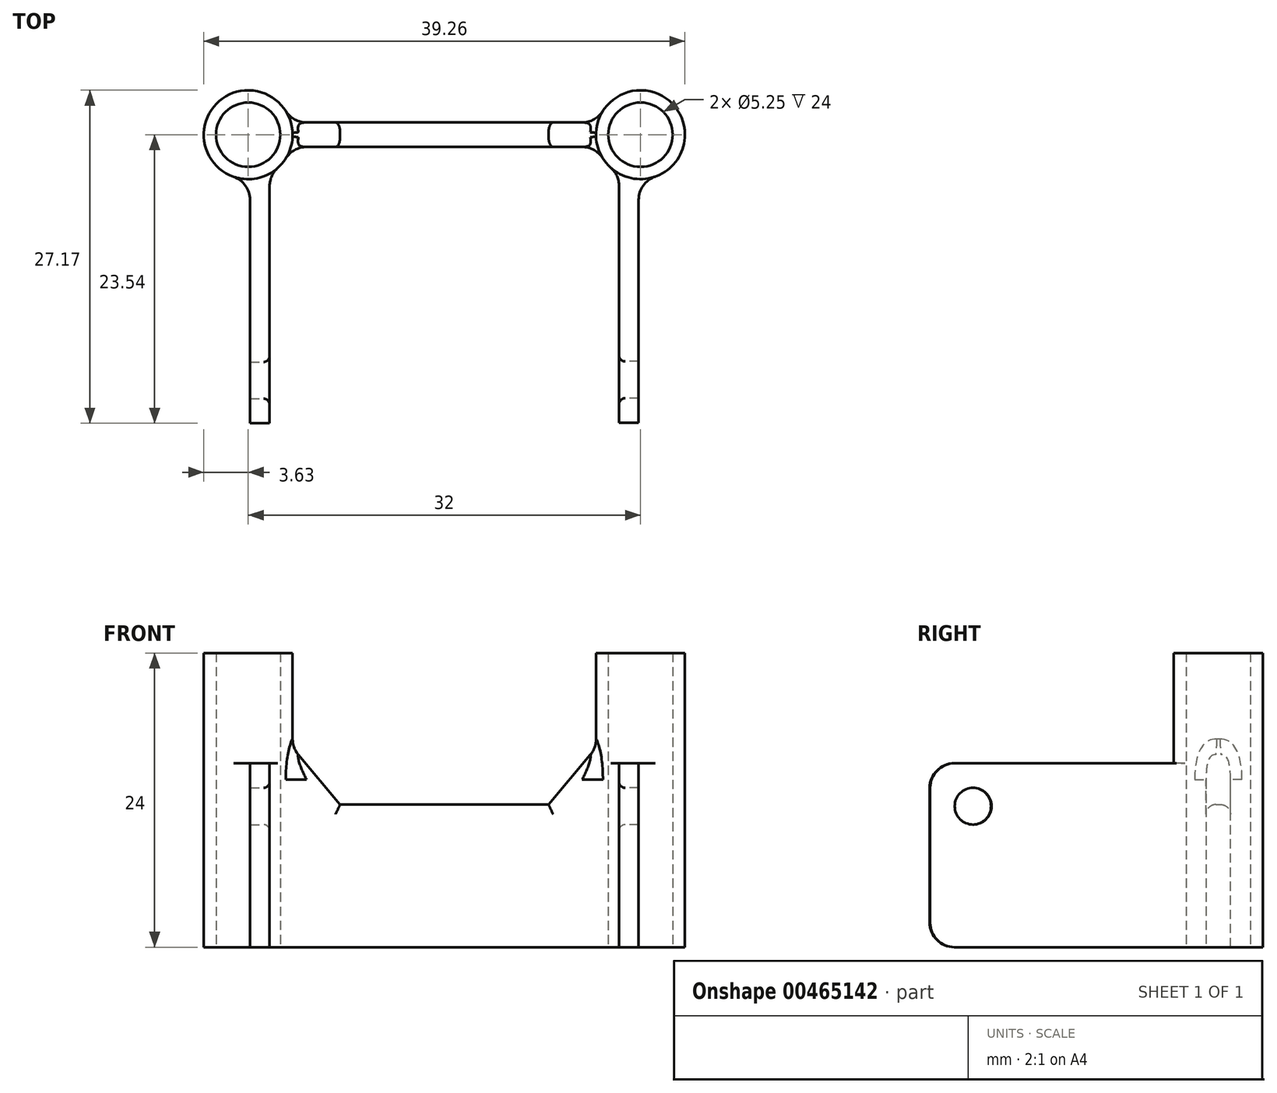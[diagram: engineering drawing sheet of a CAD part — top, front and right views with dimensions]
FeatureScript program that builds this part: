
annotation { "Feature Type Name" : "Feature", "Feature Type Description" : "" }
export const myFeature = defineFeature(function(context is Context, id is Id, definition is map)
    precondition{}
    {
        {
            var Q0;
            Q0=qCreatedBy(makeId("Top.planeOp"),FACE);
            var sketch = newSketch(context, id + "F0", { "sketchPlane" : qUnion([Q0])});
            skCircle(sketch, "E0", {"center": v(-16, 0) * mm, "radius": 3.62 * mm});
            skCircle(sketch, "E1", {"center": v(16, 0) * mm, "radius": 3.62 * mm});
            skSolve(sketch);
        }
        {
            var Q0;
            Q0=qSketchRegion(id+"F0",true);
            extrude(context, id + "F1", {"entities" : qUnion([Q0]), "depth" : 24 * mm});
        }
        {
            var Q0;
            Q0=qCreatedBy(makeId("Front.planeOp"),FACE);
            var sketch = newSketch(context, id + "F2", { "sketchPlane" : qUnion([Q0])});
            skLineSegment(sketch, "E2", {"start": v(13, 0) * mm, "end": v(13, 17) * mm});
            skLineSegment(sketch, "E3", {"start": v(13, 17) * mm, "end": v(13, 17) * mm});
            skLineSegment(sketch, "E4", {"start": v(13, 17) * mm, "end": v(8.5, 11.64) * mm});
            skLineSegment(sketch, "E5", {"start": v(8.5, 11.64) * mm, "end": v(-8.5, 11.64) * mm});
            skLineSegment(sketch, "E6", {"start": v(-8.5, 11.64) * mm, "end": v(-13, 17) * mm});
            skLineSegment(sketch, "E7", {"start": v(-13, 17) * mm, "end": v(-13, 0) * mm});
            skLineSegment(sketch, "E8", {"start": v(-13, 0) * mm, "end": v(13, 0) * mm});
            skSolve(sketch);
        }
        {
            var Q0;
            Q0=makeQuery(id+"F2.imprint","IMPRINT",FACE,{"disambiguationData":[TD([[makeQuery(id+"F2.imprint","IMPRINT",EDGE,{"derivedFrom":sQuery(id+"F2.wireOp",EDGE,"E2")}),1.0]])]});
            extrude(context, id + "F3", {"entities" : qUnion([Q0]), "endBound" : BoundingType.SYMMETRIC, "depth" : 2 * mm});
        }
        {
            var Q0;
            Q0=qCreatedBy(makeId("Right.planeOp"),FACE);
            var Q1;
            Q1=qBodyType(qCreatedBy(id+"F5",EDGE),BodyType.WIRE);
            cPlane(context, id + "F4", {"entities" : qUnion([Q0, Q1]), "cplaneType" : CPlaneType.OFFSET, "offset" : 14.25 * mm, "width" : 150 * mm, "height" : 150 * mm});
        }
        {
            var Q0;
            Q0=qCreatedBy(id+"F4.planeOp",FACE);
            var sketch = newSketch(context, id + "F5", { "sketchPlane" : qUnion([Q0])});
            skCircle(sketch, "E9", {"center": v(-20, 11.5) * mm, "radius": 1.5 * mm});
            skLineSegment(sketch, "E10", {"start": v(0, 0) * mm, "end": v(-21.5, 0) * mm});
            skLineSegment(sketch, "E11", {"start": v(-23.5, 2) * mm, "end": v(-23.5, 13) * mm});
            skLineSegment(sketch, "E12", {"start": v(-21.5, 15) * mm, "end": v(0, 15) * mm});
            skLineSegment(sketch, "E13", {"start": v(0, 15) * mm, "end": v(0, 0) * mm});
            skPoint(sketch, "E14.visualSharp", {"position": v(-23.5, 15) * mm});
            skArc(sketch, "E14.filletArc", {"start": v(-21.5, 15) * mm, "mid": v(-22.91, 14.41) * mm, "end": v(-23.5, 13) * mm});
            skPoint(sketch, "E15.visualSharp", {"position": v(-23.5, 0) * mm});
            skArc(sketch, "E15.filletArc", {"start": v(-23.5, 2) * mm, "mid": v(-22.91, 0.59) * mm, "end": v(-21.5, 0) * mm});
            skSolve(sketch);
        }
        {
            var Q0;
            Q0=qSketchRegion(id+"F5",true);
            extrude(context, id + "F6", {"entities" : qUnion([Q0]), "operationType" : NewBodyOperationType.ADD, "depth" : 1.6 * mm});
        }
        {
            var Q0;
            Q0=qCreatedBy(makeId("Right.planeOp"),FACE);
            cPlane(context, id + "F7", {"entities" : qUnion([Q0]), "cplaneType" : CPlaneType.OFFSET, "offset" : 14.25 * mm, "oppositeDirection" : true, "width" : 150 * mm, "height" : 150 * mm});
        }
        {
            var Q0;
            Q0=qCreatedBy(id+"F7.planeOp",FACE);
            var sketch = newSketch(context, id + "F8", { "sketchPlane" : qUnion([Q0])});
            skCircle(sketch, "E16", {"center": v(-20.04, 11.5) * mm, "radius": 1.5 * mm});
            skLineSegment(sketch, "E17", {"start": v(-0.04, 0) * mm, "end": v(-21.54, 0) * mm});
            skLineSegment(sketch, "E18", {"start": v(-23.54, 2) * mm, "end": v(-23.54, 13) * mm});
            skLineSegment(sketch, "E19", {"start": v(-21.54, 15) * mm, "end": v(-0.04, 15) * mm});
            skLineSegment(sketch, "E20", {"start": v(-0.04, 15) * mm, "end": v(-0.04, 0) * mm});
            skPoint(sketch, "E21.visualSharp", {"position": v(-23.54, 15) * mm});
            skArc(sketch, "E21.filletArc", {"start": v(-21.54, 15) * mm, "mid": v(-22.95, 14.41) * mm, "end": v(-23.54, 13) * mm});
            skPoint(sketch, "E22.visualSharp", {"position": v(-23.54, 0) * mm});
            skArc(sketch, "E22.filletArc", {"start": v(-23.54, 2) * mm, "mid": v(-22.95, 0.59) * mm, "end": v(-21.54, 0) * mm});
            skSolve(sketch);
        }
        {
            var Q0;
            Q0=qSketchRegion(id+"F8",true);
            extrude(context, id + "F9", {"entities" : qUnion([Q0]), "operationType" : NewBodyOperationType.ADD, "oppositeDirection" : true, "depth" : 1.6 * mm});
        }
        {
            var Q0;
            Q0=qCreatedBy(makeId("Top.planeOp"),FACE);
            var sketch = newSketch(context, id + "F10", { "sketchPlane" : qUnion([Q0])});
            skCircle(sketch, "E23", {"center": v(-16, 0) * mm, "radius": 0.5 * mm});
            skCircle(sketch, "E24", {"center": v(16, 0) * mm, "radius": 1.75 * mm});
            skSolve(sketch);
        }
        {
            var Q0;
            Q0=sQuery(id+"F10.wireOp",VERTEX,"E23.center");
            var Q1;
            Q1=sQuery(id+"F10.wireOp",VERTEX,"E24.center");
            var Q2;
            Q2=makeQuery(id+"F1.opExtrude","SWEPT_BODY",BODY,{"disambiguationData":[OSD([sQuery(id+"F0.wireOp",EDGE,"E0")])]});
            var Q3;
            Q3=makeQuery(id+"F3.opExtrude","SWEPT_BODY",BODY,{"disambiguationData":[OSD([sQuery(id+"F2.wireOp",EDGE,"in345Lub-D59E-tOme-60dj-Cq3KucnByxKd"),sQuery(id+"F2.wireOp",EDGE,"E2"),sQuery(id+"F2.wireOp",EDGE,"E4"),sQuery(id+"F2.wireOp",EDGE,"E5"),sQuery(id+"F2.wireOp",EDGE,"E6"),sQuery(id+"F2.wireOp",EDGE,"E7")])]});
            var Q4;
            Q4=makeQuery(id+"FYRTTrcSvXfLMjP_3.opExtrude","SWEPT_BODY",BODY,{"disambiguationData":[OSD([sQuery(id+"Fs8EBPNxBlUYa75_3.wireOp",EDGE,"JWLeMf17-8jiZ-tYXv-UtJK-ccR32AaEOkmf.bottom"),sQuery(id+"Fs8EBPNxBlUYa75_3.wireOp",EDGE,"JWLeMf17-8jiZ-tYXv-UtJK-ccR32AaEOkmf.top"),sQuery(id+"Fs8EBPNxBlUYa75_3.wireOp",EDGE,"JWLeMf17-8jiZ-tYXv-UtJK-ccR32AaEOkmf.left"),sQuery(id+"Fs8EBPNxBlUYa75_3.wireOp",EDGE,"JWLeMf17-8jiZ-tYXv-UtJK-ccR32AaEOkmf.right")])]});
            var Q5;
            Q5=makeQuery(id+"F1.opExtrude","SWEPT_BODY",BODY,{"disambiguationData":[OSD([sQuery(id+"F0.wireOp",EDGE,"E1")])]});
            var Q6;
            Q6=makeQuery(id+"FYRTTrcSvXfLMjP_3.opExtrude","SWEPT_BODY",BODY,{"disambiguationData":[OSD([sQuery(id+"Fs8EBPNxBlUYa75_3.wireOp",EDGE,"dHJZYZbQ-VqZX-6sAW-GdeU-ZCC2gI22Ho79.bottom"),sQuery(id+"Fs8EBPNxBlUYa75_3.wireOp",EDGE,"dHJZYZbQ-VqZX-6sAW-GdeU-ZCC2gI22Ho79.top"),sQuery(id+"Fs8EBPNxBlUYa75_3.wireOp",EDGE,"dHJZYZbQ-VqZX-6sAW-GdeU-ZCC2gI22Ho79.left"),sQuery(id+"Fs8EBPNxBlUYa75_3.wireOp",EDGE,"dHJZYZbQ-VqZX-6sAW-GdeU-ZCC2gI22Ho79.right")])]});
            hole(context, id + "F11", {"style" : HoleStyle.SIMPLE, "endStyle" : HoleEndStyle.THROUGH, "oppositeDirection" : true, "holeDiameter" : 5.25 * mm, "majorDiameter" : 5 * mm, "isTappedThrough" : true, "tappedDepth" : 12 * mm, "tapClearance" : 3, "locations" : qUnion([Q0, Q1]), "scope" : qUnion([Q2, Q3, Q4, Q5, Q6])});
        }
        {
            var Q0;
            Q0=makeQuery(id+"F1.opExtrude","SWEPT_BODY",BODY,{"disambiguationData":[OSD([sQuery(id+"F0.wireOp",EDGE,"E1")])]});
            var Q1;
            Q1=makeQuery(id+"F3.opExtrude","SWEPT_BODY",BODY,{"disambiguationData":[OSD([sQuery(id+"F2.wireOp",EDGE,"in345Lub-D59E-tOme-60dj-Cq3KucnByxKd"),sQuery(id+"F2.wireOp",EDGE,"E2"),sQuery(id+"F2.wireOp",EDGE,"E4"),sQuery(id+"F2.wireOp",EDGE,"E5"),sQuery(id+"F2.wireOp",EDGE,"E6"),sQuery(id+"F2.wireOp",EDGE,"E7")])]});
            var Q2;
            Q2=makeQuery(id+"F1.opExtrude","SWEPT_BODY",BODY,{"disambiguationData":[OSD([sQuery(id+"F0.wireOp",EDGE,"E0")])]});
            booleanBodies(context, id + "F12", {"operationType" : BooleanOperationType.UNION, "tools" : qUnion([Q0, Q1, Q2])});
        }
        {
            var Q0;
            Q0=makeQuery(id+"F3.opExtrude","CAP_EDGE",EDGE,{"disambiguationData":[OSD([sQuery(id+"F2.wireOp",EDGE,"E5")])],"isStart":false});
            var Q1;
            Q1=makeQuery(id+"F3.opExtrude","CAP_EDGE",EDGE,{"disambiguationData":[OSD([sQuery(id+"F2.wireOp",EDGE,"E5")])],"isStart":true});
            var Q2;
            Q2=makeQuery(id+"F3.opExtrude","CAP_EDGE",EDGE,{"disambiguationData":[OSD([sQuery(id+"F2.wireOp",EDGE,"E6")])],"isStart":false});
            var Q3;
            Q3=makeQuery(id+"F3.opExtrude","CAP_EDGE",EDGE,{"disambiguationData":[OSD([sQuery(id+"F2.wireOp",EDGE,"E6")])],"isStart":true});
            var Q4;
            Q4=makeQuery(id+"F3.opExtrude","CAP_EDGE",EDGE,{"disambiguationData":[OSD([sQuery(id+"F2.wireOp",EDGE,"E4")])],"isStart":false});
            var Q5;
            Q5=makeQuery(id+"F3.opExtrude","CAP_EDGE",EDGE,{"disambiguationData":[OSD([sQuery(id+"F2.wireOp",EDGE,"E4")])],"isStart":true});
            fillet(context, id + "F13", {"entities" : qUnion([Q0, Q1, Q2, Q3, Q4, Q5]), "radius" : .8 * mm, "tangentPropagation" : true, "allowEdgeOverflow" : false});
        }
        {
            var Q0;
            Q0=makeQuery(id+"F11.hole-0.boolean.opBoolean","INTERSECT",EDGE,{"derivedFrom":[makeQuery(id+"F1.opExtrude","CAP_FACE",FACE,{"disambiguationData":[OSD([sQuery(id+"F0.wireOp",EDGE,"E0")])],"isStart":false}),makeQuery(id+"F11.hole-0.opRevolve","SWEPT_FACE",FACE,{"disambiguationData":[OSD([sQuery(id+"F11.hole-0.sketch.wireOp",EDGE,"core_line_2")])]})]});
            var Q1;
            Q1=makeQuery(id+"F11.hole-1.boolean.opBoolean","INTERSECT",EDGE,{"derivedFrom":[makeQuery(id+"F1.opExtrude","CAP_FACE",FACE,{"disambiguationData":[OSD([sQuery(id+"F0.wireOp",EDGE,"E1")])],"isStart":false}),makeQuery(id+"F11.hole-1.opRevolve","SWEPT_FACE",FACE,{"disambiguationData":[OSD([sQuery(id+"F11.hole-1.sketch.wireOp",EDGE,"core_line_2")])]})]});
            var Q2;
            Q2=makeQuery(id+"F9.opExtrude","CAP_EDGE",EDGE,{"disambiguationData":[OSD([sQuery(id+"F8.wireOp",EDGE,"E16")])],"isStart":true});
            var Q3;
            Q3=makeQuery(id+"F6.opExtrude","CAP_EDGE",EDGE,{"disambiguationData":[OSD([sQuery(id+"F5.wireOp",EDGE,"E9")])],"isStart":true});
            fillet(context, id + "F14", {"entities" : qUnion([Q0, Q1, Q2, Q3]), "radius" : .5 * mm, "tangentPropagation" : true, "allowEdgeOverflow" : false});
        }
        {
            var Q0;
            Q0=makeQuery(id+"F6.boolean.opBoolean","INTERSECT",EDGE,{"derivedFrom":[makeQuery(id+"F1.opExtrude","SWEPT_FACE",FACE,{"disambiguationData":[OSD([sQuery(id+"F0.wireOp",EDGE,"E1")])]}),makeQuery(id+"F6.opExtrude","CAP_FACE",FACE,{"disambiguationData":[OSD([sQuery(id+"F5.wireOp",EDGE,"E9"),sQuery(id+"F5.wireOp",EDGE,"E10"),sQuery(id+"F5.wireOp",EDGE,"E11"),sQuery(id+"F5.wireOp",EDGE,"E12"),sQuery(id+"F5.wireOp",EDGE,"E13"),sQuery(id+"F5.wireOp",EDGE,"E14.filletArc"),sQuery(id+"F5.wireOp",EDGE,"E15.filletArc")])],"isStart":true})]});
            var Q1;
            Q1=makeQuery(id+"F6.boolean.opBoolean","INTERSECT",EDGE,{"derivedFrom":[makeQuery(id+"F1.opExtrude","SWEPT_FACE",FACE,{"disambiguationData":[OSD([sQuery(id+"F0.wireOp",EDGE,"E1")])]}),makeQuery(id+"F6.opExtrude","CAP_FACE",FACE,{"disambiguationData":[OSD([sQuery(id+"F5.wireOp",EDGE,"E9"),sQuery(id+"F5.wireOp",EDGE,"E10"),sQuery(id+"F5.wireOp",EDGE,"E11"),sQuery(id+"F5.wireOp",EDGE,"E12"),sQuery(id+"F5.wireOp",EDGE,"E13"),sQuery(id+"F5.wireOp",EDGE,"E14.filletArc"),sQuery(id+"F5.wireOp",EDGE,"E15.filletArc")])],"isStart":false})]});
            var Q2;
            Q2=makeQuery(id+"F12.opBoolean","INTERSECT",EDGE,{"derivedFrom":[makeQuery(id+"F1.opExtrude","SWEPT_FACE",FACE,{"disambiguationData":[OSD([sQuery(id+"F0.wireOp",EDGE,"E1")])]}),makeQuery(id+"F3.opExtrude","CAP_FACE",FACE,{"disambiguationData":[OSD([sQuery(id+"F2.wireOp",EDGE,"E2"),sQuery(id+"F2.wireOp",EDGE,"E4"),sQuery(id+"F2.wireOp",EDGE,"E5"),sQuery(id+"F2.wireOp",EDGE,"E6"),sQuery(id+"F2.wireOp",EDGE,"E7"),sQuery(id+"F2.wireOp",EDGE,"E8")])],"isStart":false})]});
            var Q3;
            Q3=makeQuery(id+"F12.opBoolean","INTERSECT",EDGE,{"derivedFrom":[makeQuery(id+"F1.opExtrude","SWEPT_FACE",FACE,{"disambiguationData":[OSD([sQuery(id+"F0.wireOp",EDGE,"E0")])]}),makeQuery(id+"F3.opExtrude","CAP_FACE",FACE,{"disambiguationData":[OSD([sQuery(id+"F2.wireOp",EDGE,"E2"),sQuery(id+"F2.wireOp",EDGE,"E4"),sQuery(id+"F2.wireOp",EDGE,"E5"),sQuery(id+"F2.wireOp",EDGE,"E6"),sQuery(id+"F2.wireOp",EDGE,"E7"),sQuery(id+"F2.wireOp",EDGE,"E8")])],"isStart":false})]});
            var Q4;
            Q4=makeQuery(id+"F9.boolean.opBoolean","INTERSECT",EDGE,{"derivedFrom":[makeQuery(id+"F1.opExtrude","SWEPT_FACE",FACE,{"disambiguationData":[OSD([sQuery(id+"F0.wireOp",EDGE,"E0")])]}),makeQuery(id+"F9.opExtrude","CAP_FACE",FACE,{"disambiguationData":[OSD([sQuery(id+"F8.wireOp",EDGE,"E16"),sQuery(id+"F8.wireOp",EDGE,"E17"),sQuery(id+"F8.wireOp",EDGE,"E18"),sQuery(id+"F8.wireOp",EDGE,"E19"),sQuery(id+"F8.wireOp",EDGE,"E20"),sQuery(id+"F8.wireOp",EDGE,"E21.filletArc"),sQuery(id+"F8.wireOp",EDGE,"E22.filletArc")])],"isStart":false})]});
            var Q5;
            Q5=makeQuery(id+"F9.boolean.opBoolean","INTERSECT",EDGE,{"derivedFrom":[makeQuery(id+"F1.opExtrude","SWEPT_FACE",FACE,{"disambiguationData":[OSD([sQuery(id+"F0.wireOp",EDGE,"E0")])]}),makeQuery(id+"F9.opExtrude","CAP_FACE",FACE,{"disambiguationData":[OSD([sQuery(id+"F8.wireOp",EDGE,"E16"),sQuery(id+"F8.wireOp",EDGE,"E17"),sQuery(id+"F8.wireOp",EDGE,"E18"),sQuery(id+"F8.wireOp",EDGE,"E19"),sQuery(id+"F8.wireOp",EDGE,"E20"),sQuery(id+"F8.wireOp",EDGE,"E21.filletArc"),sQuery(id+"F8.wireOp",EDGE,"E22.filletArc")])],"isStart":true})]});
            fillet(context, id + "F15", {"entities" : qUnion([Q0, Q1, Q2, Q3, Q4, Q5]), "radius" : 2 * mm, "tangentPropagation" : true, "allowEdgeOverflow" : false});
        }
    });
